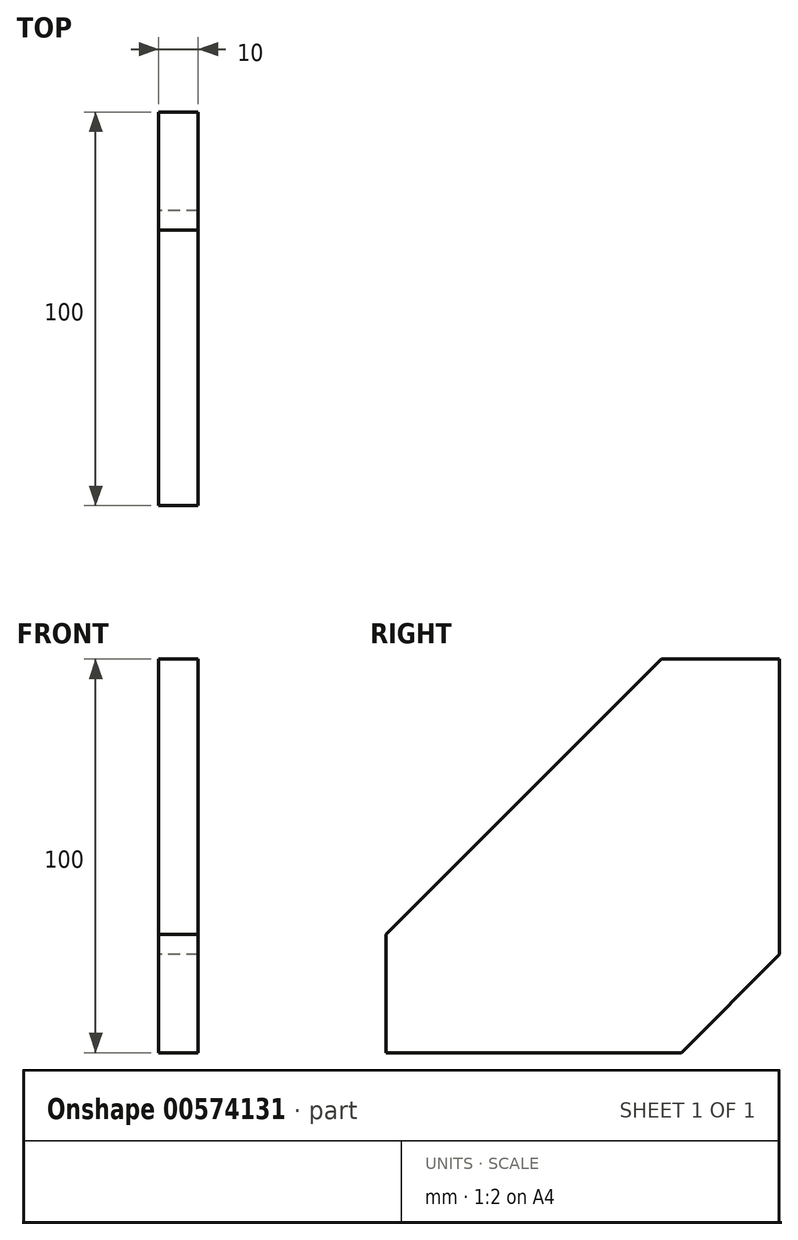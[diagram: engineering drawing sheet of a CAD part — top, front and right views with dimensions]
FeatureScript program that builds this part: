
annotation { "Feature Type Name" : "Feature", "Feature Type Description" : "" }
export const myFeature = defineFeature(function(context is Context, id is Id, definition is map)
    precondition{}
    {
        {
            var Q0;
            Q0=qCreatedBy(makeId("Right.planeOp"),FACE);
            var sketch = newSketch(context, id + "F0", { "sketchPlane" : qUnion([Q0])});
            skLineSegment(sketch, "E0", {"start": v(25, -50) * mm, "end": v(-50, -50) * mm});
            skLineSegment(sketch, "E1", {"start": v(-50, -50) * mm, "end": v(-50, -20) * mm});
            skLineSegment(sketch, "E2", {"start": v(-50, -20) * mm, "end": v(20, 50) * mm});
            skLineSegment(sketch, "E3", {"start": v(20, 50) * mm, "end": v(50, 50) * mm});
            skLineSegment(sketch, "E4", {"start": v(50, 50) * mm, "end": v(50, -25) * mm});
            skLineSegment(sketch, "E5", {"start": v(50, -25) * mm, "end": v(25, -50) * mm});
            skSolve(sketch);
        }
        {
            var Q0;
            Q0=makeQuery(id+"F0.imprint","IMPRINT",FACE,{"disambiguationData":[TD([[makeQuery(id+"F0.imprint","IMPRINT",EDGE,{"derivedFrom":sQuery(id+"F0.wireOp",EDGE,"E0")}),-1.0]])]});
            extrude(context, id + "F1", {"entities" : qUnion([Q0]), "depth" : 10 * mm, "offsetDistance" : 25 * mm});
        }
    });
